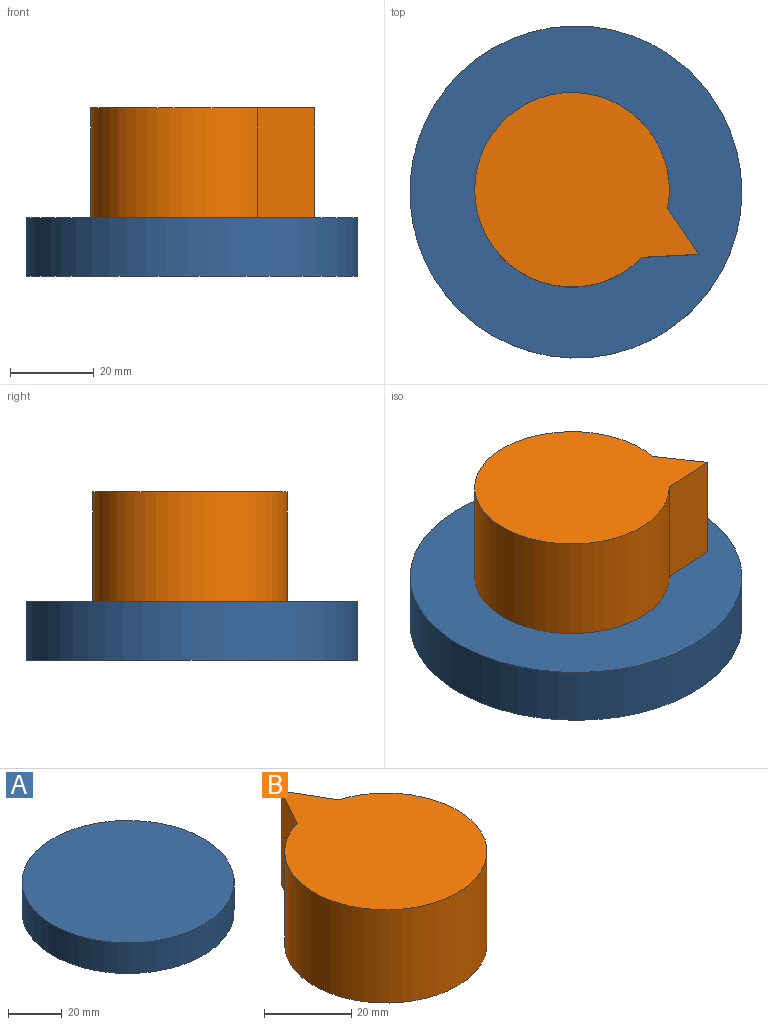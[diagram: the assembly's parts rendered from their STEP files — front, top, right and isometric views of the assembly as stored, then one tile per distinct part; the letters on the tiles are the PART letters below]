
ASSEMBLY  parts=2 mates=1
PART A: 3 faces, bbox 79.2x79.2x14 mm
  f0: cylinder r=39.6mm len=79.21mm, axis (0,0,-1), area 3476.2mm2, adj f1,f2
  f1: plane 79.21x79.21mm, normal (0,0,1), area 4927.4mm2, adj f0
  f2: plane 79.21x79.21mm, normal (0,0,-1), area 4927.4mm2, adj f0
PART B: 5 faces, bbox 46.4x57.2x26.2 mm
  f0: cylinder r=23.2mm len=46.4mm, axis (0,0,-1), area 3464.2mm2, adj f1,f2,f3,f4
  f1: plane 26.16x11.79mm, normal (0.87,0.5,0), area 356.1mm2, adj f0,f2,f3,f4
  f2: plane 26.16x11.67mm, normal (-0.88,0.48,0), area 347.9mm2, adj f0,f1,f3,f4
  f3: plane 57.17x46.4mm, normal (0,0,1), area 1760.1mm2, adj f0,f1,f2
  f4: plane 57.17x46.4mm, normal (0,0,-1), area 1760.1mm2, adj f0,f1,f2
PLACE A t=(-10.88,1.38,-1.58)mm fixed
PLACE B rot(axis=(0,0,-1),116.9deg) t=(-11.81,1.86,12.39)mm
MATE revolute A.f0 <-> B.f4  axis (0,0,1) through (-10.88,1.38,12.39)mm
